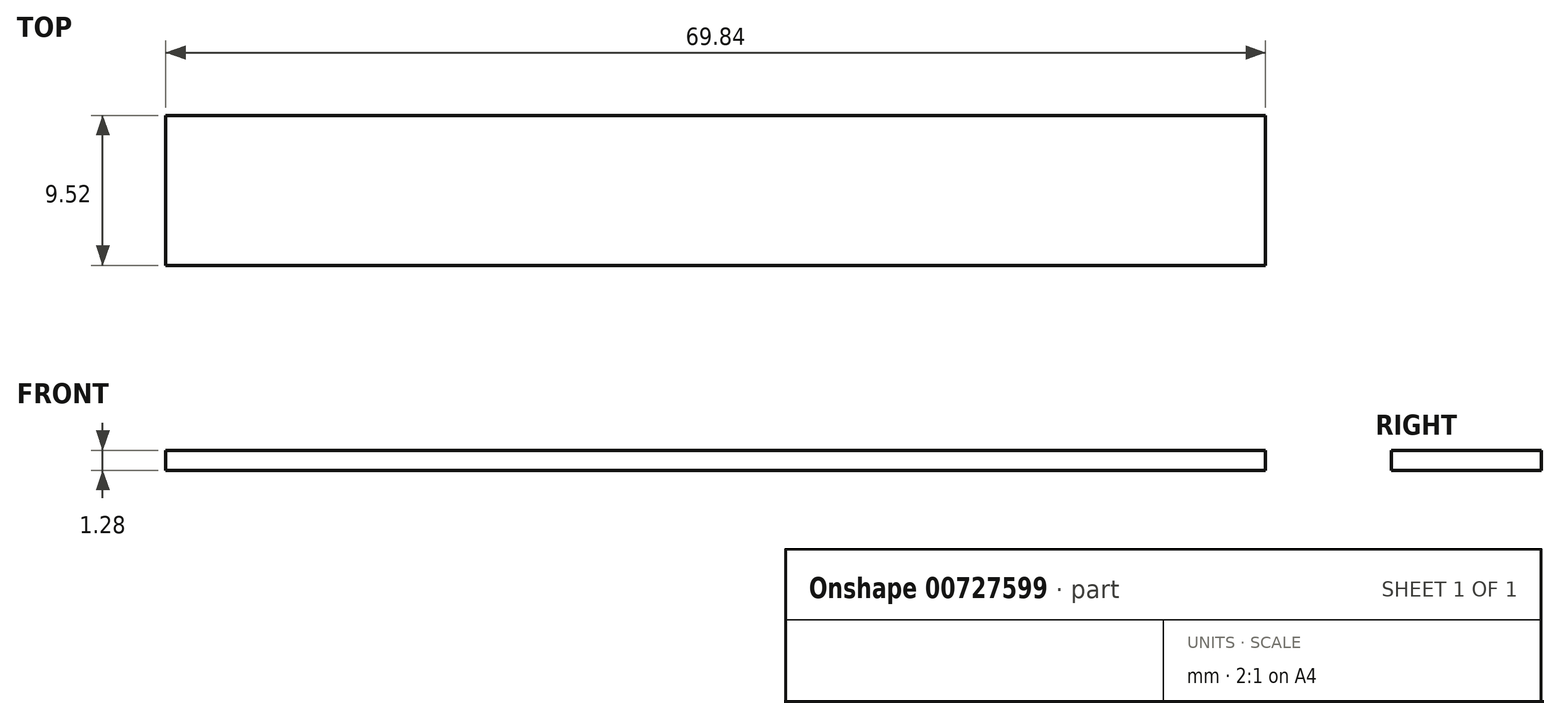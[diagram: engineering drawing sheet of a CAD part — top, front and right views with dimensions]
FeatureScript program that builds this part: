
annotation { "Feature Type Name" : "Feature", "Feature Type Description" : "" }
export const myFeature = defineFeature(function(context is Context, id is Id, definition is map)
    precondition{}
    {
        {
            var Q0;
            Q0=qCreatedBy(makeId("Top.planeOp"),FACE);
            var sketch = newSketch(context, id + "F0", { "sketchPlane" : qUnion([Q0])});
            skLineSegment(sketch, "E0.bottom", {"start": v(34.92, 4.76) * mm, "end": v(-34.92, 4.76) * mm});
            skLineSegment(sketch, "E0.top", {"start": v(34.92, -4.76) * mm, "end": v(-34.92, -4.76) * mm});
            skLineSegment(sketch, "E0.left", {"start": v(34.92, 4.76) * mm, "end": v(34.92, -4.76) * mm});
            skLineSegment(sketch, "E0.right", {"start": v(-34.92, 4.76) * mm, "end": v(-34.92, -4.76) * mm});
            skPoint(sketch, "E0.middle", {"position": v(0, 0) * mm});
            skSolve(sketch);
        }
        {
            var Q0;
            Q0 = qSketchRegion(id + "F0", true);
            extrude(context, id + "F1", {"entities" : qUnion([Q0]), "endBound" : BoundingType.SYMMETRIC, "depth" : 1.27 * mm, "offsetDistance" : 25.4 * mm});
        }
    });
